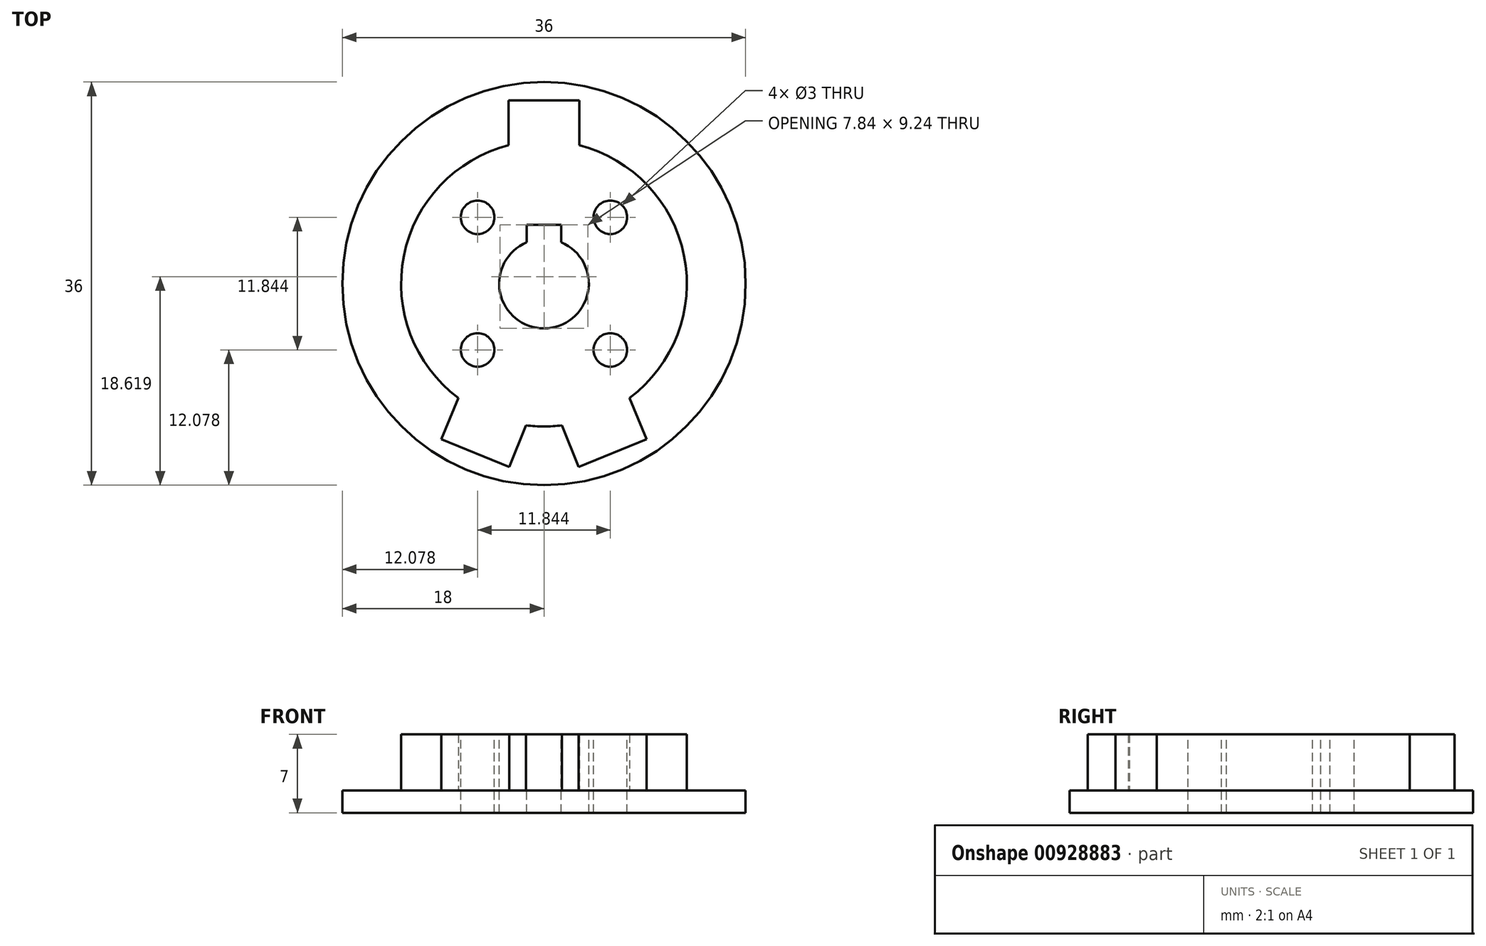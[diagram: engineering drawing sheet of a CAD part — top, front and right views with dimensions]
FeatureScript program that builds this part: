
annotation { "Feature Type Name" : "Feature", "Feature Type Description" : "" }
export const myFeature = defineFeature(function(context is Context, id is Id, definition is map)
    precondition{}
    {
        {
            var Q0;
            Q0=qCreatedBy(makeId("Top.planeOp"),FACE);
            var sketch = newSketch(context, id + "F0", { "sketchPlane" : qUnion([Q0])});
            skArc(sketch, "E0", {"start": v(7.65, -10.2) * mm, "mid": v(12.5, 2.5) * mm, "end": v(3.15, 12.35) * mm});
            skLineSegment(sketch, "E1", {"start": v(0, 12.75) * mm, "end": v(0, -12.75) * mm, "construction": true});
            skLineSegment(sketch, "E2", {"start": v(-3.15, 16.35) * mm, "end": v(0, 16.35) * mm});
            skLineSegment(sketch, "E3", {"start": v(0, 16.35) * mm, "end": v(3.15, 16.35) * mm});
            skLineSegment(sketch, "E4", {"start": v(-3.15, 16.35) * mm, "end": v(-3.15, 12.35) * mm});
            skLineSegment(sketch, "E5", {"start": v(3.15, 16.35) * mm, "end": v(3.15, 12.35) * mm});
            skLineSegment(sketch, "E6", {"start": v(1.6, -12.65) * mm, "end": v(7.65, -10.2) * mm, "construction": true});
            skLineSegment(sketch, "E7", {"start": v(1.6, -12.65) * mm, "end": v(3.1, -16.36) * mm});
            skLineSegment(sketch, "E8", {"start": v(7.65, -10.2) * mm, "end": v(9.15, -13.9) * mm});
            skLineSegment(sketch, "E9", {"start": v(3.1, -16.36) * mm, "end": v(9.15, -13.9) * mm});
            skLineSegment(sketch, "E10.MirrorCS", {"start": v(-1.6, -12.65) * mm, "end": v(-3.1, -16.36) * mm});
            skLineSegment(sketch, "E11.MirrorCS", {"start": v(-3.1, -16.36) * mm, "end": v(-9.15, -13.9) * mm});
            skLineSegment(sketch, "E12.MirrorCS", {"start": v(-7.65, -10.2) * mm, "end": v(-9.15, -13.9) * mm});
            skArc(sketch, "E13.trimOffspring", {"start": v(-1.6, -12.65) * mm, "mid": v(0, -12.75) * mm, "end": v(1.6, -12.65) * mm});
            skArc(sketch, "E14.trimOffspring", {"start": v(-3.15, 12.35) * mm, "mid": v(-12.5, 2.5) * mm, "end": v(-7.65, -10.2) * mm});
            skLineSegment(sketch, "E15", {"start": v(-1.6, -12.65) * mm, "end": v(1.6, -12.65) * mm, "construction": true});
            skLineSegment(sketch, "E16", {"start": v(-3.1, -16.36) * mm, "end": v(3.1, -16.36) * mm, "construction": true});
            skLineSegment(sketch, "E17", {"start": v(-9.15, -13.9) * mm, "end": v(9.15, -13.9) * mm, "construction": true});
            skLineSegment(sketch, "E18", {"start": v(-7.65, -10.2) * mm, "end": v(7.65, -10.2) * mm, "construction": true});
            skSolve(sketch);
        }
        {
            var Q0;
            Q0=qSketchRegion(id+"F0",true);
            extrude(context, id + "F1", {"entities" : qUnion([Q0]), "depth" : 5 * mm, "offsetDistance" : 25 * mm});
        }
        {
            var Q0;
            Q0=makeQuery(id+"F1.opExtrude","CAP_FACE",FACE,{"disambiguationData":[OSD([sQuery(id+"F0.wireOp",EDGE,"E0"),sQuery(id+"F0.wireOp",EDGE,"E2"),sQuery(id+"F0.wireOp",EDGE,"E3"),sQuery(id+"F0.wireOp",EDGE,"E4"),sQuery(id+"F0.wireOp",EDGE,"E5"),sQuery(id+"F0.wireOp",EDGE,"E7"),sQuery(id+"F0.wireOp",EDGE,"E8"),sQuery(id+"F0.wireOp",EDGE,"E9"),sQuery(id+"F0.wireOp",EDGE,"E10.MirrorCS"),sQuery(id+"F0.wireOp",EDGE,"E11.MirrorCS"),sQuery(id+"F0.wireOp",EDGE,"E12.MirrorCS"),sQuery(id+"F0.wireOp",EDGE,"E13.trimOffspring"),sQuery(id+"F0.wireOp",EDGE,"E14.trimOffspring")])],"isStart":true});
            var sketch = newSketch(context, id + "F2", { "sketchPlane" : qUnion([Q0])});
            skCircle(sketch, "E19", {"center": v(0, 0) * mm, "radius": 18 * mm});
            skSolve(sketch);
        }
        {
            var Q0;
            Q0=qSketchRegion(id+"F2",true);
            extrude(context, id + "F3", {"entities" : qUnion([Q0]), "operationType" : NewBodyOperationType.ADD, "depth" : 2 * mm, "offsetDistance" : 25 * mm});
        }
        {
            var Q0;
            Q0=makeQuery(id+"F1.opExtrude","CAP_FACE",FACE,{"disambiguationData":[OSD([sQuery(id+"F0.wireOp",EDGE,"E0"),sQuery(id+"F0.wireOp",EDGE,"E2"),sQuery(id+"F0.wireOp",EDGE,"E3"),sQuery(id+"F0.wireOp",EDGE,"E4"),sQuery(id+"F0.wireOp",EDGE,"E5"),sQuery(id+"F0.wireOp",EDGE,"E7"),sQuery(id+"F0.wireOp",EDGE,"E8"),sQuery(id+"F0.wireOp",EDGE,"E9"),sQuery(id+"F0.wireOp",EDGE,"E10.MirrorCS"),sQuery(id+"F0.wireOp",EDGE,"E11.MirrorCS"),sQuery(id+"F0.wireOp",EDGE,"E12.MirrorCS"),sQuery(id+"F0.wireOp",EDGE,"E13.trimOffspring"),sQuery(id+"F0.wireOp",EDGE,"E14.trimOffspring")])],"isStart":false});
            var sketch = newSketch(context, id + "F4", { "sketchPlane" : qUnion([Q0])});
            skArc(sketch, "E20", {"start": v(-1.55, 3.69) * mm, "mid": v(0, -4) * mm, "end": v(1.55, 3.69) * mm});
            skLineSegment(sketch, "E21", {"start": v(0, 4) * mm, "end": v(0, 5.24) * mm, "construction": true});
            skLineSegment(sketch, "E22", {"start": v(0, 5.24) * mm, "end": v(1.55, 5.24) * mm});
            skLineSegment(sketch, "E23", {"start": v(0, 5.24) * mm, "end": v(-1.55, 5.24) * mm});
            skLineSegment(sketch, "E24", {"start": v(1.55, 5.24) * mm, "end": v(1.55, 3.69) * mm});
            skLineSegment(sketch, "E25", {"start": v(-1.55, 5.24) * mm, "end": v(-1.55, 3.69) * mm});
            skLineSegment(sketch, "E26", {"start": v(-12.75, 0) * mm, "end": v(0, 0) * mm, "construction": true});
            skLineSegment(sketch, "E27", {"start": v(0, 0) * mm, "end": v(-2.83, 2.83) * mm, "construction": true});
            skLineSegment(sketch, "E28", {"start": v(0, 0) * mm, "end": v(8.84, -8.84) * mm, "construction": true});
            skLineSegment(sketch, "E29.MirrorCS", {"start": v(0, 0) * mm, "end": v(8.84, 8.84) * mm, "construction": true});
            skLineSegment(sketch, "E30.MirrorCS", {"start": v(0, 0) * mm, "end": v(-9.02, -9.02) * mm, "construction": true});
            skCircle(sketch, "E31", {"center": v(-5.92, 5.92) * mm, "radius": 1.5 * mm});
            skCircle(sketch, "E32.1.0", {"center": v(-5.92, -5.92) * mm, "radius": 1.5 * mm});
            skCircle(sketch, "E32.2.0", {"center": v(5.92, -5.92) * mm, "radius": 1.5 * mm});
            skCircle(sketch, "E32.3.0", {"center": v(5.92, 5.92) * mm, "radius": 1.5 * mm});
            skLineSegment(sketch, "E33", {"start": v(-2.83, 2.83) * mm, "end": v(-9.02, 9.02) * mm, "construction": true});
            skSolve(sketch);
        }
        {
            var Q0;
            Q0=qSketchRegion(id+"F4",true);
            var Q1;
            Q1=makeQuery(id+"F3.opExtrude","CAP_FACE",FACE,{"disambiguationData":[OSD([sQuery(id+"F2.wireOp",EDGE,"E19")])],"isStart":false});
            extrude(context, id + "F5", {"entities" : qUnion([Q0]), "operationType" : NewBodyOperationType.REMOVE, "endBound" : BoundingType.UP_TO_SURFACE, "oppositeDirection" : true, "depth" : 25 * mm, "endBoundEntityFace" : qUnion([Q1]), "offsetDistance" : 25 * mm});
        }
    });
